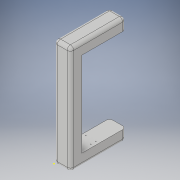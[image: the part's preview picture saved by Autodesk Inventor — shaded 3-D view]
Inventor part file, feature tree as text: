
AUTODESK INVENTOR PART (.ipt)
format: ipt  version: 2018 (Build 220112000, 112)  size: 199,168 bytes
history: native  units: in
note: dims shown in document units (in); Inventor stores cm internally (conversion verified against a paired STEP export)
features: sketch x6, extrude x5, fillet x1
ambient origin geometry x8: Origin, YZ Plane, XZ Plane, XY Plane, X Axis, Y Axis, Z Axis, Center Point
bodies: Solid1 (feature_tree)
feature tree (12):
  sketch  "Sketch1"  dims[d0=26.0in d1=13.5in d2=13.5in]
  extrude  "Extrusion1"  Depth=13.5in
  fillet  "Fillet1"  Radius=13.5in
  extrude  "Extrusion2"  Depth=3.5in
  extrude  "Extrusion3"  Depth=5.0in TaperAngle=0.0deg
  extrude  "Extrusion5"  Depth=1.0in
  extrude  "Extrusion6"  Depth=0.125in TaperAngle=0.0deg
  sketch  "Sketch2"  dims[d3=3.5in d4=3.5in]
  sketch  "Sketch3"  dims[d5=3.5in d6=5.0in d7=0.0in]
  sketch  "Sketch4"  dims[d8=1.0in d9=10.0in]
  sketch  "Sketch5"  dims[d10=6.0in d14=0.125in d15=0.0in]
  sketch  "Sketch6"  dims[d23=1.5in d24=1.5in d25=1.5in d26=11.5in d27=3.0in d28=1.5in d30=1.5in d31=0.2in d32=0.125in d33=0.0in d34=3.438in d36=3.438in d37=0.2in d40=2.0in d41=0.125in d42=0.0in d46=1.5in d47=0.2in d48=0.125in d49=0.0in d50=1.5in d51=1.5in]
